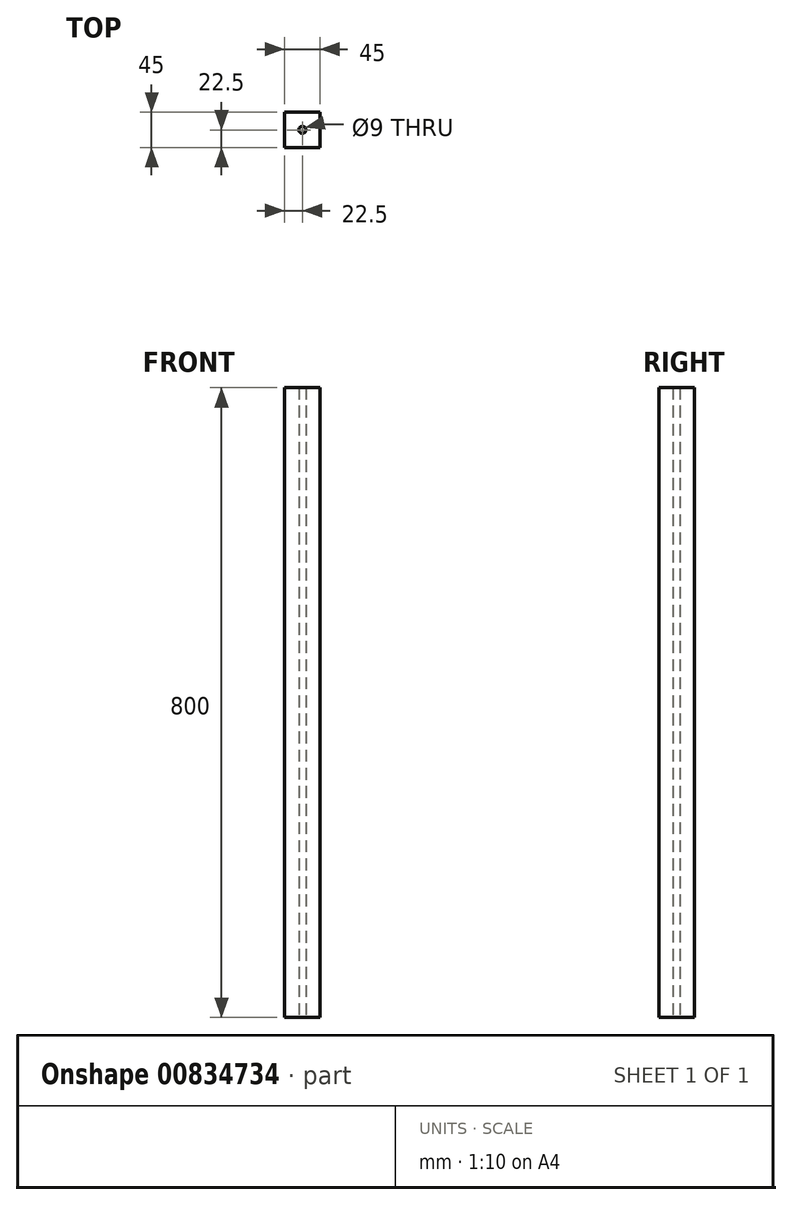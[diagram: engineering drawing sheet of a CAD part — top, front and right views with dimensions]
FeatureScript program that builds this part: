
annotation { "Feature Type Name" : "Feature", "Feature Type Description" : "" }
export const myFeature = defineFeature(function(context is Context, id is Id, definition is map)
    precondition{}
    {
        {
            var Q0;
            Q0=qCreatedBy(makeId("Top.planeOp"),FACE);
            var sketch = newSketch(context, id + "F0", { "sketchPlane" : qUnion([Q0])});
            skLineSegment(sketch, "E0.bottom", {"start": v(-22.5, 22.5) * mm, "end": v(22.5, 22.5) * mm});
            skLineSegment(sketch, "E0.top", {"start": v(-22.5, -22.5) * mm, "end": v(22.5, -22.5) * mm});
            skLineSegment(sketch, "E0.left", {"start": v(-22.5, 22.5) * mm, "end": v(-22.5, -22.5) * mm});
            skLineSegment(sketch, "E0.right", {"start": v(22.5, 22.5) * mm, "end": v(22.5, -22.5) * mm});
            skPoint(sketch, "E0.middle", {"position": v(0, 0) * mm});
            skCircle(sketch, "E1", {"center": v(0, 0) * mm, "radius": 4.5 * mm});
            skSolve(sketch);
        }
        {
            var Q0;
            Q0=makeQuery(id+"F0.imprint","IMPRINT",FACE,{"disambiguationData":[TD([[makeQuery(id+"F0.imprint","IMPRINT",EDGE,{"derivedFrom":sQuery(id+"F0.wireOp",EDGE,"E0.bottom")}),-1.0]])]});
            extrude(context, id + "F1", {"entities" : qUnion([Q0]), "depth" : 800 * mm, "offsetDistance" : 25 * mm});
        }
    });
